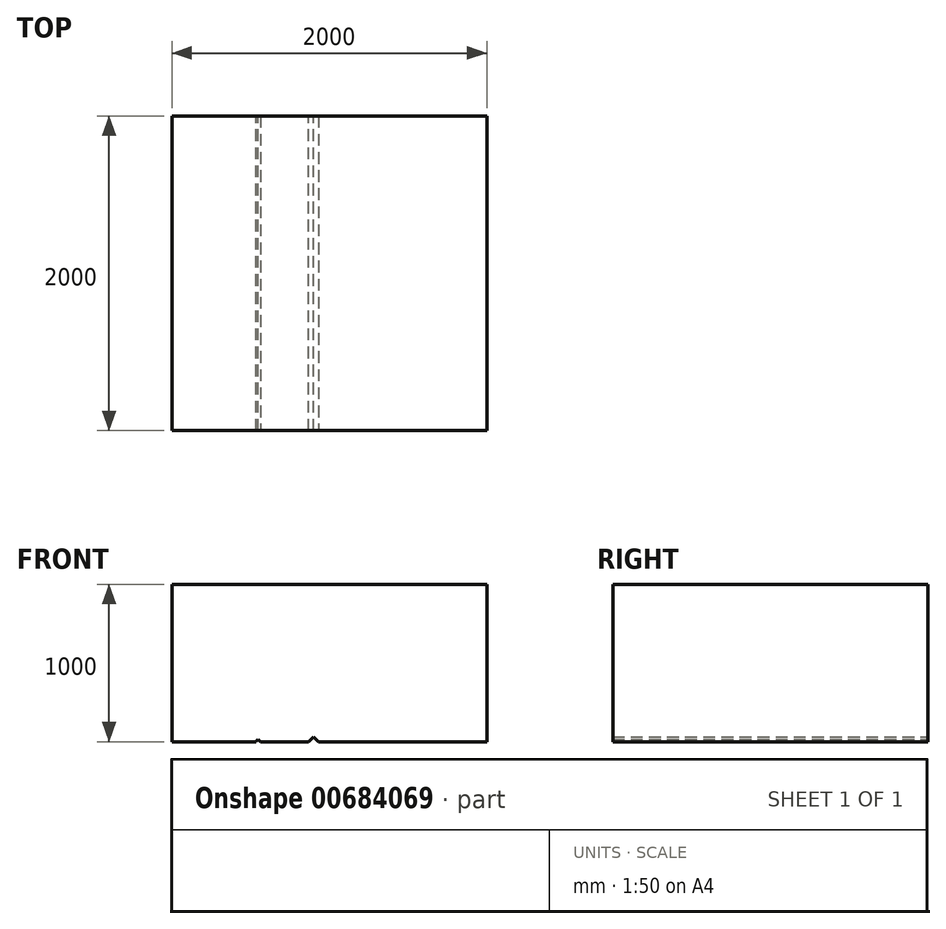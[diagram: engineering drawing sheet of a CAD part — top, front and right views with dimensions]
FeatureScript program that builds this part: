
annotation { "Feature Type Name" : "Feature", "Feature Type Description" : "" }
export const myFeature = defineFeature(function(context is Context, id is Id, definition is map)
    precondition{}
    {
        {
            var Q0;
            Q0=qCreatedBy(makeId("Front.planeOp"),FACE);
            var sketch = newSketch(context, id + "F0", { "sketchPlane" : qUnion([Q0])});
            skLineSegment(sketch, "E0.bottom", {"start": v(1000, 500) * mm, "end": v(-1000, 500) * mm});
            skLineSegment(sketch, "E0.top", {"start": v(1000, -500) * mm, "end": v(-1000, -500) * mm});
            skLineSegment(sketch, "E0.left", {"start": v(1000, 500) * mm, "end": v(1000, -500) * mm});
            skLineSegment(sketch, "E0.right", {"start": v(-1000, 500) * mm, "end": v(-1000, -500) * mm});
            skPoint(sketch, "E0.middle", {"position": v(0, 0) * mm});
            skSolve(sketch);
        }
        {
            var Q0;
            Q0=makeQuery(id+"F0.imprint","IMPRINT",FACE,{"disambiguationData":[TD([[makeQuery(id+"F0.imprint","IMPRINT",EDGE,{"derivedFrom":sQuery(id+"F0.wireOp",EDGE,"E0.bottom")}),1.0]])]});
            var sketch = newSketch(context, id + "F1", { "sketchPlane" : qUnion([Q0])});
            skLineSegment(sketch, "E1", {"start": v(-466.5, -498.8) * mm, "end": v(-452.15, -484.45) * mm});
            skLineSegment(sketch, "E2", {"start": v(-452.15, -484.45) * mm, "end": v(-434.93, -501.67) * mm});
            skLineSegment(sketch, "E3", {"start": v(-434.93, -501.67) * mm, "end": v(-134.93, -501.67) * mm});
            skLineSegment(sketch, "E4", {"start": v(-134.93, -501.67) * mm, "end": v(-99.04, -468.66) * mm});
            skLineSegment(sketch, "E5", {"start": v(-99.04, -468.66) * mm, "end": v(-68.67, -501.67) * mm});
            skLineSegment(sketch, "E6", {"start": v(-68.67, -501.67) * mm, "end": v(-68.67, -553.35) * mm});
            skLineSegment(sketch, "E7", {"start": v(-68.67, -553.35) * mm, "end": v(-469.38, -553.35) * mm});
            skLineSegment(sketch, "E8", {"start": v(-469.38, -553.35) * mm, "end": v(-466.5, -498.8) * mm});
            skSolve(sketch);
        }
        {
            var Q0;
            Q0=makeQuery(id+"F0.imprint","IMPRINT",FACE,{"disambiguationData":[TD([[makeQuery(id+"F0.imprint","IMPRINT",EDGE,{"derivedFrom":sQuery(id+"F0.wireOp",EDGE,"E0.bottom")}),1.0]])]});
            extrude(context, id + "F2", {"entities" : qUnion([Q0]), "depth" : 2000 * mm, "offsetDistance" : 25 * mm});
        }
        {
            var Q0;
            Q0 = qSketchRegion(id + "F1", true);
            extrude(context, id + "F3", {"entities" : qUnion([Q0]), "operationType" : NewBodyOperationType.REMOVE, "depth" : 2000 * mm, "offsetDistance" : 25 * mm});
        }
    });
